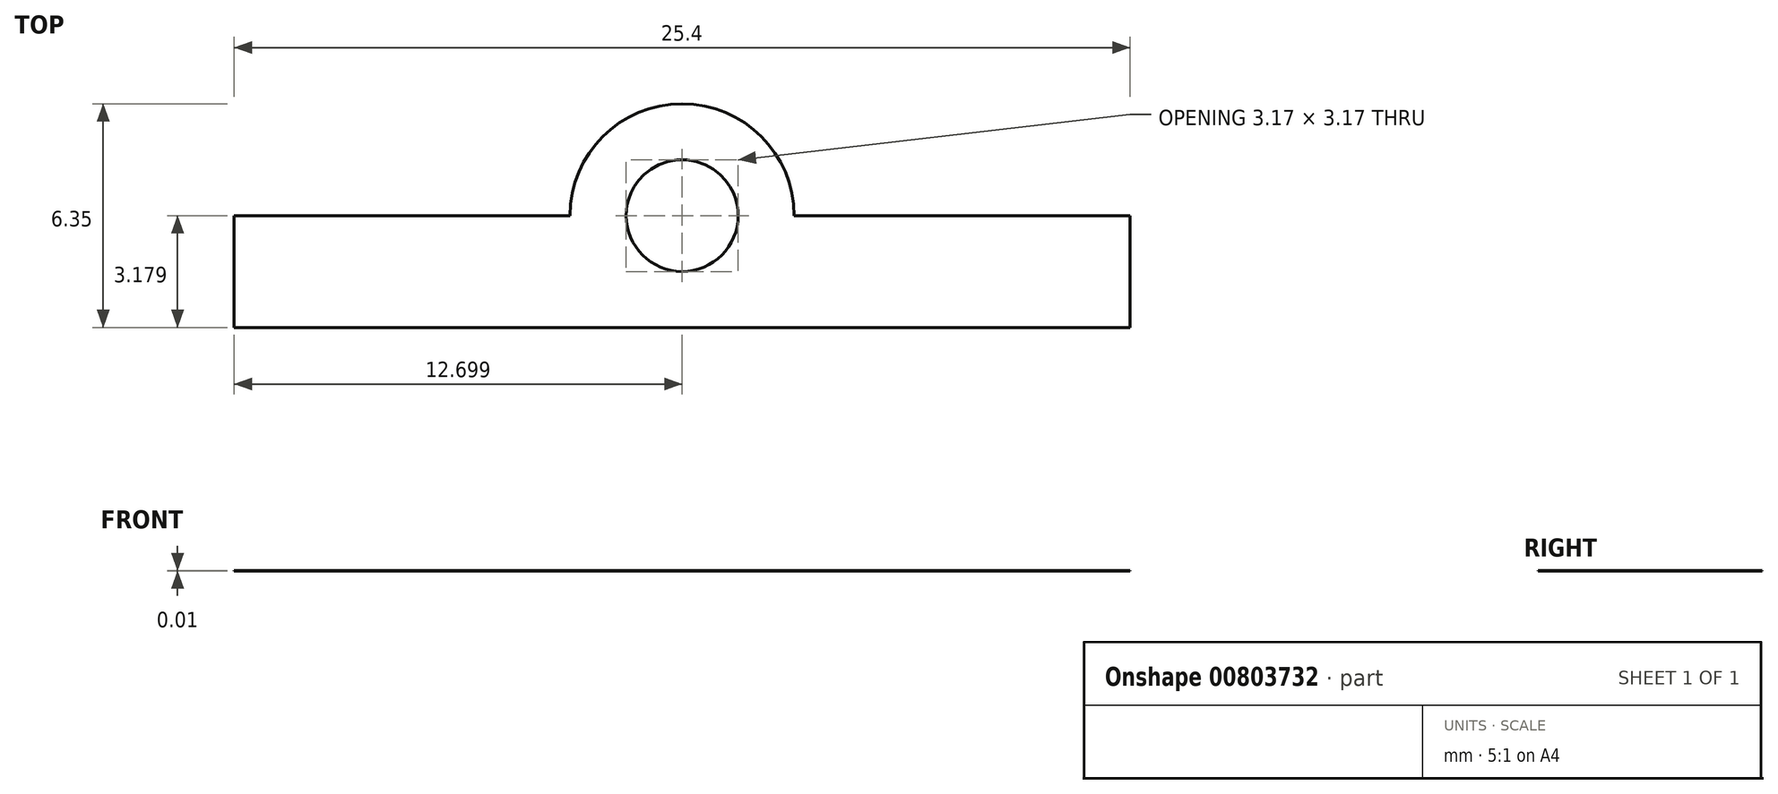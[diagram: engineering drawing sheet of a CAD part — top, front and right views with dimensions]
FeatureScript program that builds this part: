
annotation { "Feature Type Name" : "Feature", "Feature Type Description" : "" }
export const myFeature = defineFeature(function(context is Context, id is Id, definition is map)
    precondition{}
    {
        {
            var Q0;
            Q0=qCreatedBy(makeId("Top.planeOp"),FACE);
            var sketch = newSketch(context, id + "F0", { "sketchPlane" : qUnion([Q0])});
            skLineSegment(sketch, "E0.top", {"start": v(-5.01, -4.4) * mm, "end": v(20.39, -4.4) * mm});
            skLineSegment(sketch, "E0.left", {"start": v(-5.01, -1.23) * mm, "end": v(-5.01, -4.4) * mm});
            skLineSegment(sketch, "E0.right", {"start": v(20.39, -1.23) * mm, "end": v(20.39, -4.4) * mm});
            skLineSegment(sketch, "E1.bottom", {"start": v(4.51, -1.23) * mm, "end": v(10.86, -1.23) * mm});
            skLineSegment(sketch, "E1.top", {"start": v(7.69, 1.94) * mm, "end": v(7.69, 1.94) * mm});
            skLineSegment(sketch, "E1.left", {"start": v(4.51, -1.23) * mm, "end": v(4.51, -1.23) * mm});
            skLineSegment(sketch, "E1.right", {"start": v(10.86, -1.23) * mm, "end": v(10.86, -1.23) * mm});
            skCircle(sketch, "E2", {"center": v(7.69, -1.23) * mm, "radius": 1.59 * mm});
            skPoint(sketch, "E2.centerSnap0", {"position": v(7.69, -1.23) * mm});
            skLineSegment(sketch, "E3", {"start": v(4.51, -1.23) * mm, "end": v(-5.01, -1.23) * mm});
            skLineSegment(sketch, "E4", {"start": v(10.86, -1.23) * mm, "end": v(20.39, -1.23) * mm});
            skPoint(sketch, "E5.visualSharp", {"position": v(4.51, 1.94) * mm});
            skArc(sketch, "E5.filletArc", {"start": v(7.69, 1.94) * mm, "mid": v(5.44, 1.01) * mm, "end": v(4.51, -1.23) * mm});
            skPoint(sketch, "E6.visualSharp", {"position": v(10.86, 1.94) * mm});
            skArc(sketch, "E6.filletArc", {"start": v(10.86, -1.23) * mm, "mid": v(9.93, 1.01) * mm, "end": v(7.69, 1.94) * mm});
            skSolve(sketch);
        }
        {
            var Q0;
            Q0=makeQuery(id+"F0.imprint","IMPRINT",FACE,{"disambiguationData":[TD([[makeQuery(id+"F0.imprint","IMPRINT",EDGE,{"derivedFrom":sQuery(id+"F0.wireOp",EDGE,"E1.bottom")}),1.0]])]});
            var Q1;
            Q1=makeQuery(id+"F0.imprint","IMPRINT",FACE,{"disambiguationData":[TD([[makeQuery(id+"F0.imprint","IMPRINT",EDGE,{"derivedFrom":sQuery(id+"F0.wireOp",EDGE,"E0.top")}),1.0]])]});
            extrude(context, id + "F1", {"entities" : qUnion([Q0, Q1]), "depth" : .75 / 50.8 * mm, "offsetDistance" : 25.4 * mm});
        }
        {
            var Q0;
            Q0=makeQuery(id+"F1.opExtrude","SWEPT_FACE",FACE,{"disambiguationData":[OSD([sQuery(id+"F0.wireOp",EDGE,"E4")])]});
            var sketch = newSketch(context, id + "F2", { "sketchPlane" : qUnion([Q0])});
            skLineSegment(sketch, "E7", {"start": v(-20.39, 4.76) * mm, "end": v(-10.86, 4.76) * mm});
            skPoint(sketch, "E8", {"position": v(-15.63, 4.76) * mm});
            skSolve(sketch);
        }
        {
            var Q0;
            Q0=sQuery(id+"F2.wireOp",VERTEX,"E8");
            var Q1;
            Q1=makeQuery(id+"F1.opExtrude","SWEPT_BODY",BODY,{"disambiguationData":[OSD([sQuery(id+"F0.wireOp",EDGE,"E0.top"),sQuery(id+"F0.wireOp",EDGE,"E0.left"),sQuery(id+"F0.wireOp",EDGE,"E0.right"),sQuery(id+"F0.wireOp",EDGE,"E1.left"),sQuery(id+"F0.wireOp",EDGE,"E1.right"),sQuery(id+"F0.wireOp",EDGE,"E2"),sQuery(id+"F0.wireOp",EDGE,"E3"),sQuery(id+"F0.wireOp",EDGE,"E4"),sQuery(id+"F0.wireOp",EDGE,"E5.filletArc"),sQuery(id+"F0.wireOp",EDGE,"E6.filletArc")])]});
            hole(context, id + "F3", {"style" : HoleStyle.SIMPLE, "endStyle" : HoleEndStyle.THROUGH, "holeDiameter" : 3.17 * mm, "majorDiameter" : 6.35 * mm, "isTappedThrough" : true, "tappedDepth" : 12.7 * mm, "tapClearance" : 3, "locations" : qUnion([Q0]), "scope" : qUnion([Q1])});
        }
        {
            var Q0;
            Q0=makeQuery(id+"F1.opExtrude","SWEPT_FACE",FACE,{"disambiguationData":[OSD([sQuery(id+"F0.wireOp",EDGE,"E3")])]});
            var sketch = newSketch(context, id + "F4", { "sketchPlane" : qUnion([Q0])});
            skLineSegment(sketch, "E9", {"start": v(-4.51, 4.76) * mm, "end": v(5.01, 4.76) * mm});
            skPoint(sketch, "E10", {"position": v(0.25, 4.76) * mm});
            skSolve(sketch);
        }
        {
            var Q0;
            Q0=sQuery(id+"F4.wireOp",VERTEX,"E10");
            var Q1;
            Q1=makeQuery(id+"F1.opExtrude","SWEPT_BODY",BODY,{"disambiguationData":[OSD([sQuery(id+"F0.wireOp",EDGE,"E0.top"),sQuery(id+"F0.wireOp",EDGE,"E0.left"),sQuery(id+"F0.wireOp",EDGE,"E0.right"),sQuery(id+"F0.wireOp",EDGE,"E1.left"),sQuery(id+"F0.wireOp",EDGE,"E1.right"),sQuery(id+"F0.wireOp",EDGE,"E2"),sQuery(id+"F0.wireOp",EDGE,"E3"),sQuery(id+"F0.wireOp",EDGE,"E4"),sQuery(id+"F0.wireOp",EDGE,"E5.filletArc"),sQuery(id+"F0.wireOp",EDGE,"E6.filletArc")])]});
            hole(context, id + "F5", {"style" : HoleStyle.SIMPLE, "endStyle" : HoleEndStyle.THROUGH, "holeDiameter" : 3.17 * mm, "majorDiameter" : 6.35 * mm, "isTappedThrough" : true, "tappedDepth" : 12.7 * mm, "tapClearance" : 3, "locations" : qUnion([Q0]), "scope" : qUnion([Q1])});
        }
    });
